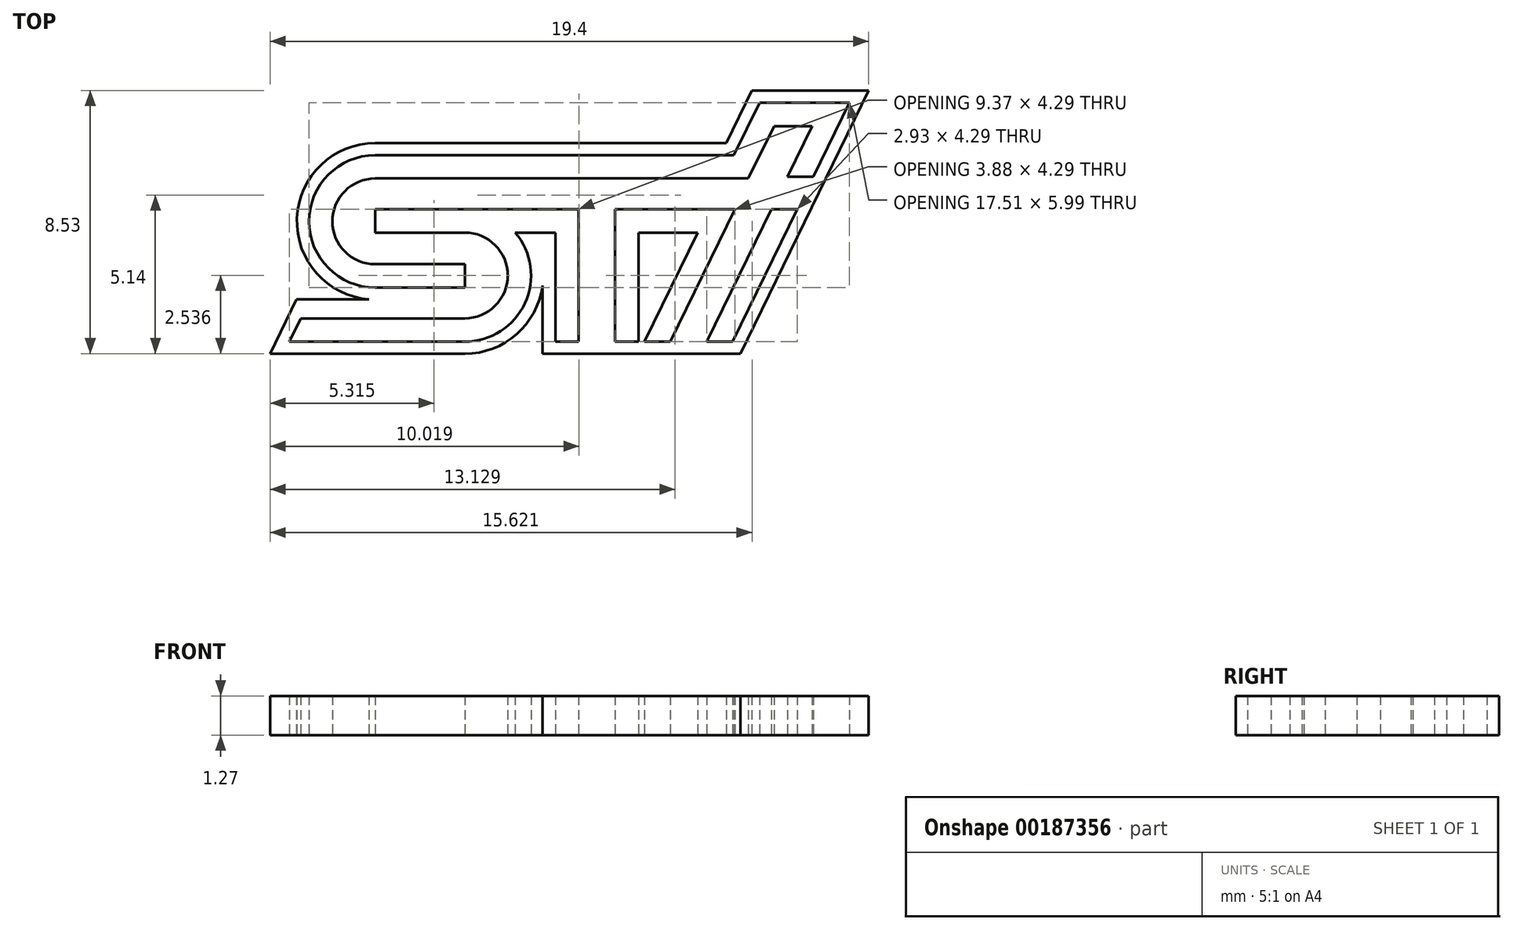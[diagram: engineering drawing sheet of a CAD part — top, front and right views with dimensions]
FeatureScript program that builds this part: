
annotation { "Feature Type Name" : "Feature", "Feature Type Description" : "" }
export const myFeature = defineFeature(function(context is Context, id is Id, definition is map)
    precondition{}
    {
        {
            var Q0;
            Q0=qCreatedBy(makeId("Top.planeOp"),FACE);
            var sketch = newSketch(context, id + "F0", { "sketchPlane" : qUnion([Q0])});
            skLineSegment(sketch, "E0", {"start": v(-60.95, -26) * mm, "end": v(-54.64, -26) * mm});
            skLineSegment(sketch, "E1", {"start": v(-60.95, -26) * mm, "end": v(-60.1, -24.24) * mm});
            skLineSegment(sketch, "E2", {"start": v(-60.1, -24.24) * mm, "end": v(-57.74, -24.24) * mm});
            skLineSegment(sketch, "E3", {"start": v(-52.12, -23.79) * mm, "end": v(-52.12, -26) * mm});
            skLineSegment(sketch, "E4", {"start": v(-52.12, -26) * mm, "end": v(-45.7, -26) * mm});
            skLineSegment(sketch, "E5", {"start": v(-45.7, -26) * mm, "end": v(-41.55, -17.47) * mm});
            skLineSegment(sketch, "E6", {"start": v(-41.55, -17.47) * mm, "end": v(-45.33, -17.47) * mm});
            skLineSegment(sketch, "E7", {"start": v(-45.33, -17.47) * mm, "end": v(-46.16, -19.17) * mm});
            skLineSegment(sketch, "E8", {"start": v(-46.16, -19.17) * mm, "end": v(-57.54, -19.17) * mm});
            skArc(sketch, "E9", {"start": v(-57.54, -19.17) * mm, "mid": v(-60.08, -21.61) * mm, "end": v(-57.74, -24.24) * mm});
            skArc(sketch, "E10", {"start": v(-54.64, -26) * mm, "mid": v(-52.96, -25.37) * mm, "end": v(-52.12, -23.79) * mm});
            skLineSegment(sketch, "E11", {"start": v(-54.64, -23.86) * mm, "end": v(-54.64, -23.1) * mm});
            skLineSegment(sketch, "E12", {"start": v(-54.64, -23.1) * mm, "end": v(-57.54, -23.1) * mm});
            skLineSegment(sketch, "E13", {"start": v(-54.64, -23.86) * mm, "end": v(-57.54, -23.86) * mm});
            skLineSegment(sketch, "E14", {"start": v(-57.54, -20.32) * mm, "end": v(-45.45, -20.32) * mm});
            skLineSegment(sketch, "E15", {"start": v(-45.45, -20.32) * mm, "end": v(-44.62, -18.62) * mm});
            skLineSegment(sketch, "E16", {"start": v(-44.62, -18.62) * mm, "end": v(-43.39, -18.62) * mm});
            skLineSegment(sketch, "E17", {"start": v(-43.39, -18.62) * mm, "end": v(-44.19, -20.26) * mm});
            skLineSegment(sketch, "E18", {"start": v(-44.19, -20.26) * mm, "end": v(-43.34, -20.26) * mm});
            skLineSegment(sketch, "E19", {"start": v(-43.34, -20.26) * mm, "end": v(-42.18, -17.86) * mm});
            skLineSegment(sketch, "E20", {"start": v(-42.18, -17.86) * mm, "end": v(-45.09, -17.86) * mm});
            skLineSegment(sketch, "E21", {"start": v(-45.09, -17.86) * mm, "end": v(-45.92, -19.56) * mm});
            skLineSegment(sketch, "E22", {"start": v(-45.92, -19.56) * mm, "end": v(-57.54, -19.56) * mm});
            skArc(sketch, "E23", {"start": v(-57.54, -19.56) * mm, "mid": v(-59.69, -21.71) * mm, "end": v(-57.54, -23.86) * mm});
            skArc(sketch, "E24", {"start": v(-57.54, -20.32) * mm, "mid": v(-58.93, -21.71) * mm, "end": v(-57.54, -23.1) * mm});
            skLineSegment(sketch, "E25", {"start": v(-60.32, -25.61) * mm, "end": v(-54.64, -25.61) * mm});
            skLineSegment(sketch, "E26", {"start": v(-60.32, -25.61) * mm, "end": v(-59.95, -24.85) * mm});
            skLineSegment(sketch, "E27", {"start": v(-59.95, -24.85) * mm, "end": v(-54.64, -24.85) * mm});
            skLineSegment(sketch, "E28", {"start": v(-54.64, -22.07) * mm, "end": v(-57.54, -22.07) * mm});
            skLineSegment(sketch, "E29", {"start": v(-57.54, -22.07) * mm, "end": v(-57.54, -21.32) * mm});
            skLineSegment(sketch, "E30", {"start": v(-57.54, -21.32) * mm, "end": v(-50.95, -21.32) * mm});
            skLineSegment(sketch, "E31", {"start": v(-50.95, -21.32) * mm, "end": v(-50.95, -25.61) * mm});
            skLineSegment(sketch, "E32", {"start": v(-50.95, -25.61) * mm, "end": v(-51.7, -25.61) * mm});
            skLineSegment(sketch, "E33", {"start": v(-51.7, -25.61) * mm, "end": v(-51.7, -22.07) * mm});
            skLineSegment(sketch, "E34", {"start": v(-51.7, -22.07) * mm, "end": v(-53, -22.07) * mm});
            skArc(sketch, "E35", {"start": v(-54.64, -24.85) * mm, "mid": v(-53.25, -23.46) * mm, "end": v(-54.64, -22.07) * mm});
            skArc(sketch, "E36", {"start": v(-54.64, -25.61) * mm, "mid": v(-52.69, -24.36) * mm, "end": v(-53, -22.07) * mm});
            skLineSegment(sketch, "E37", {"start": v(-49.76, -25.61) * mm, "end": v(-49, -25.61) * mm});
            skLineSegment(sketch, "E38", {"start": v(-49, -25.61) * mm, "end": v(-49, -22.07) * mm});
            skLineSegment(sketch, "E39", {"start": v(-49, -22.07) * mm, "end": v(-47.09, -22.07) * mm});
            skLineSegment(sketch, "E40", {"start": v(-47.09, -22.07) * mm, "end": v(-48.81, -25.61) * mm});
            skLineSegment(sketch, "E41", {"start": v(-48.81, -25.61) * mm, "end": v(-47.97, -25.61) * mm});
            skLineSegment(sketch, "E42", {"start": v(-47.97, -25.61) * mm, "end": v(-45.88, -21.32) * mm});
            skLineSegment(sketch, "E43", {"start": v(-45.88, -21.32) * mm, "end": v(-49.76, -21.32) * mm});
            skLineSegment(sketch, "E44", {"start": v(-49.76, -21.32) * mm, "end": v(-49.76, -25.61) * mm});
            skLineSegment(sketch, "E45", {"start": v(-46.8, -25.61) * mm, "end": v(-45.96, -25.61) * mm});
            skLineSegment(sketch, "E46", {"start": v(-45.96, -25.61) * mm, "end": v(-43.86, -21.32) * mm});
            skLineSegment(sketch, "E47", {"start": v(-43.86, -21.32) * mm, "end": v(-44.7, -21.32) * mm});
            skLineSegment(sketch, "E48", {"start": v(-46.8, -25.61) * mm, "end": v(-44.7, -21.32) * mm});
            skSolve(sketch);
        }
        {
            var Q0;
            Q0=makeQuery(id+"F0.imprint","IMPRINT",FACE,{"disambiguationData":[TD([[makeQuery(id+"F0.imprint","IMPRINT",EDGE,{"derivedFrom":sQuery(id+"F0.wireOp",EDGE,"E0")}),1.0]])]});
            extrude(context, id + "F1", {"entities" : qUnion([Q0]), "depth" : 1.27 * mm});
        }
    });
